# Revit family: РБП-12-7_RV17_LOD400 (05.11.23)
name_source: partatom
category: Электрооборудование
revit_build: Autodesk Revit 2017 (Build: 20170118_1100(x64)
units: mm (PartAtom-declared; Revit-internal decimal feet)

## family parameters
Всегда вертикально = Нет
Конфигурация панели = Два столбца, слева направо
На основе рабочей плоскости = Да
Общий = Нет
При загрузке вырезать с полостями = Нет
Размер круглого соединителя = Использовать диаметр
Тип детали = Щит
Точка расчета площади = Нет

## types (1)
- РБП-12-7
    ADSK_URL страницы изделия = https://stilsoft.ru
    ADSK_Единица измерения = шт.
    ADSK_Завод-изготовитель = ООО «Основа Безопасности»
    ADSK_Количество = 1
    ADSK_Марка = СТАЕ.436121.001
    ADSK_Масса = 2.6
    ADSK_Наименование = Источник питания РБП-12-7
    ADSK_Размер_Высота = 78 мм
    ADSK_Размер_Глубина = 150 мм
    ADSK_Размер_Длина = 323 мм
    d_короба = 20 мм
    Диапазон напряжения защитного отключения АКБ, не менее, В = 10,5-11,5
    Диапазон рабочих температур, °С = от + 5 до + 50
    Напряжение = 13.8
    Отметка по умолчанию = 1219 мм
    Потребляемый ток нагрузки максимальный, А = 7 А
    Потребляемый ток нагрузки номинальный, А = 5 А
    Ток заряда АКБ, не более, А = 1 А
